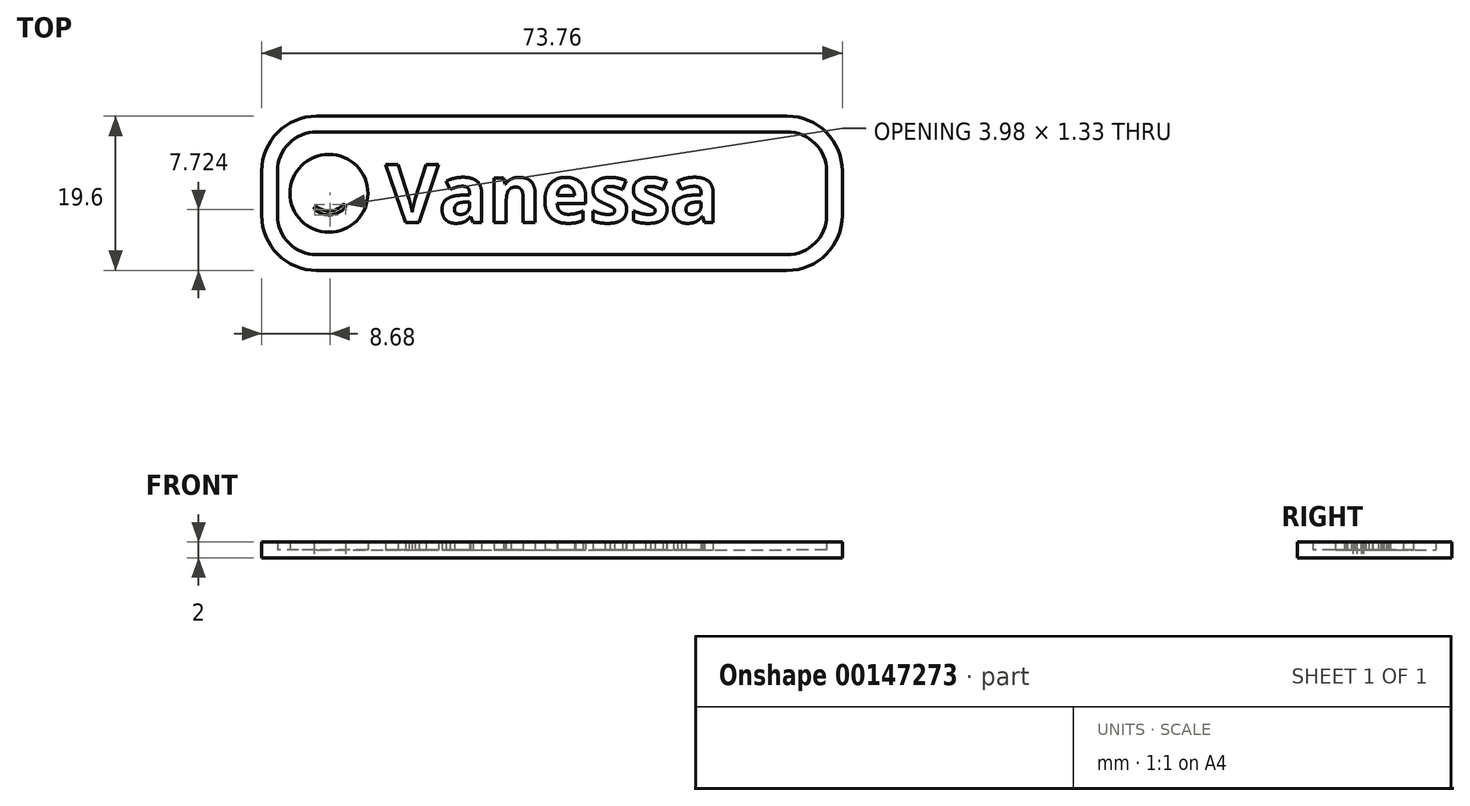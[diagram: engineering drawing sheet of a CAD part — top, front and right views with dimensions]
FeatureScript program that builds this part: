
annotation { "Feature Type Name" : "Feature", "Feature Type Description" : "" }
export const myFeature = defineFeature(function(context is Context, id is Id, definition is map)
    precondition{}
    {
        {
            var Q0;
            Q0=qCreatedBy(makeId("Top.planeOp"),FACE);
            var sketch = newSketch(context, id + "F0", { "sketchPlane" : qUnion([Q0])});
            skLineSegment(sketch, "E0.bottom", {"start": v(29.88, -7.8) * mm, "end": v(-29.88, -7.8) * mm});
            skLineSegment(sketch, "E0.top", {"start": v(29.88, 7.8) * mm, "end": v(-29.88, 7.8) * mm});
            skLineSegment(sketch, "E0.left", {"start": v(34.88, -2.8) * mm, "end": v(34.88, 2.8) * mm});
            skLineSegment(sketch, "E0.right", {"start": v(-34.88, -2.8) * mm, "end": v(-34.88, 2.8) * mm});
            skPoint(sketch, "E0.middle", {"position": v(0, 0) * mm});
            skPoint(sketch, "E1.visualSharp", {"position": v(-34.88, 7.8) * mm});
            skArc(sketch, "E1.filletArc", {"start": v(-29.88, 7.8) * mm, "mid": v(-33.41, 6.34) * mm, "end": v(-34.88, 2.8) * mm});
            skPoint(sketch, "E2.visualSharp", {"position": v(34.88, -7.8) * mm});
            skArc(sketch, "E2.filletArc", {"start": v(29.88, -7.8) * mm, "mid": v(33.41, -6.34) * mm, "end": v(34.88, -2.8) * mm});
            skPoint(sketch, "E3.visualSharp", {"position": v(34.88, 7.8) * mm});
            skArc(sketch, "E3.filletArc", {"start": v(34.88, 2.8) * mm, "mid": v(33.41, 6.34) * mm, "end": v(29.88, 7.8) * mm});
            skPoint(sketch, "E4.visualSharp", {"position": v(-34.88, -7.8) * mm});
            skArc(sketch, "E4.filletArc", {"start": v(-34.88, -2.8) * mm, "mid": v(-33.41, -6.34) * mm, "end": v(-29.88, -7.8) * mm});
            skLineSegment(sketch, "E5.0", {"start": v(29.88, 9.8) * mm, "end": v(-29.88, 9.8) * mm});
            skArc(sketch, "E5.1", {"start": v(36.88, 2.8) * mm, "mid": v(34.83, 7.75) * mm, "end": v(29.88, 9.8) * mm});
            skArc(sketch, "E5.2", {"start": v(-29.88, 9.8) * mm, "mid": v(-34.83, 7.75) * mm, "end": v(-36.88, 2.8) * mm});
            skLineSegment(sketch, "E5.3", {"start": v(36.88, -2.8) * mm, "end": v(36.88, 2.8) * mm});
            skLineSegment(sketch, "E5.4", {"start": v(-36.88, -2.8) * mm, "end": v(-36.88, 2.8) * mm});
            skArc(sketch, "E5.5", {"start": v(-36.88, -2.8) * mm, "mid": v(-34.83, -7.75) * mm, "end": v(-29.88, -9.8) * mm});
            skLineSegment(sketch, "E5.6", {"start": v(29.88, -9.8) * mm, "end": v(-29.88, -9.8) * mm});
            skArc(sketch, "E5.7", {"start": v(29.88, -9.8) * mm, "mid": v(34.83, -7.75) * mm, "end": v(36.88, -2.8) * mm});
            skText(sketch, "E6", { "text": "Vanessa", "fontName": "OpenSans-Bold.ttf"});
            skLineSegment(sketch, "E7", {"start": v(-21.12, 0) * mm, "end": v(21.12, 0) * mm, "construction": true});
            skCircle(sketch, "E8", {"center": v(-28.33, 0) * mm, "radius": 4.35 * mm});
            skLineSegment(sketch, "E9", {"start": v(-32.35, 1.65) * mm, "end": v(-24.3, 1.65) * mm, "construction": true});
            skCircle(sketch, "E10", {"center": v(-30.35, 1.65) * mm, "radius": 0.6 * mm});
            skCircle(sketch, "E11", {"center": v(-26.23, 1.65) * mm, "radius": 0.6 * mm});
            skArc(sketch, "E12", {"start": v(-26.46, -1.66) * mm, "mid": v(-28.15, -2.5) * mm, "end": v(-29.94, -1.9) * mm});
            skArc(sketch, "E13.0.startCap", {"start": v(-26.64, -1.5) * mm, "mid": v(-26.3, -1.47) * mm, "end": v(-26.27, -1.82) * mm});
            skArc(sketch, "E13.0.endCap", {"start": v(-30.1, -2.1) * mm, "mid": v(-30.13, -1.75) * mm, "end": v(-29.78, -1.72) * mm});
            skArc(sketch, "E13.0.left", {"start": v(-26.27, -1.82) * mm, "mid": v(-28.13, -2.74) * mm, "end": v(-30.1, -2.1) * mm});
            skArc(sketch, "E13.0.right", {"start": v(-26.64, -1.5) * mm, "mid": v(-28.17, -2.24) * mm, "end": v(-29.78, -1.72) * mm});
            skCircle(sketch, "E14", {"center": v(-28.33, 0) * mm, "radius": 4.95 * mm});
            const initialGuessF0  = {"E6": [-0.02112, -0.00372, 1, 0, 0.00744]};
            skSetInitialGuess(sketch, initialGuessF0);
            skSolve(sketch);
        }
        {
            var Q0;
            Q0=makeQuery(id+"F0.imprint","IMPRINT",FACE,{"disambiguationData":[TD([[makeQuery(id+"F0.imprint","IMPRINT",EDGE,{"derivedFrom":sQuery(id+"F0.wireOp",EDGE,"E0.bottom")}),1.0]])]});
            var Q1;
            Q1 = qSketchRegion(id + "F0", true);
            var Q2;
            Q2=makeQuery(id+"F0.imprint","IMPRINT",FACE,{"disambiguationData":[TD([[makeQuery(id+"F0.imprint","IMPRINT",EDGE,{"derivedFrom":sQuery(id+"F0.wireOp",EDGE,"E6.sketch_text.stroke-35")}),-1.0]])]});
            var Q3;
            Q3=makeQuery(id+"F0.imprint","IMPRINT",FACE,{"disambiguationData":[TD([[makeQuery(id+"F0.imprint","IMPRINT",EDGE,{"derivedFrom":sQuery(id+"F0.wireOp",EDGE,"E6.sketch_text.stroke-142")}),1.0]])]});
            var Q4;
            Q4=makeQuery(id+"F0.imprint","IMPRINT",FACE,{"disambiguationData":[TD([[makeQuery(id+"F0.imprint","IMPRINT",EDGE,{"derivedFrom":sQuery(id+"F0.wireOp",EDGE,"E6.sketch_text.stroke-52")}),-1.0]])]});
            var Q5;
            Q5=makeQuery(id+"F0.imprint","IMPRINT",FACE,{"disambiguationData":[TD([[makeQuery(id+"F0.imprint","IMPRINT",EDGE,{"derivedFrom":sQuery(id+"F0.wireOp",EDGE,"E8")}),1.0]])]});
            var Q6;
            Q6=makeQuery(id+"F0.imprint","IMPRINT",FACE,{"disambiguationData":[TD([[makeQuery(id+"F0.imprint","IMPRINT",EDGE,{"derivedFrom":sQuery(id+"F0.wireOp",EDGE,"E6.sketch_text.stroke-98")}),-1.0]])]});
            var Q7;
            Q7=makeQuery(id+"F0.imprint","IMPRINT",FACE,{"disambiguationData":[TD([[makeQuery(id+"F0.imprint","IMPRINT",EDGE,{"derivedFrom":sQuery(id+"F0.wireOp",EDGE,"E6.sketch_text.stroke-28")}),1.0]])]});
            var Q8;
            Q8=makeQuery(id+"F0.imprint","IMPRINT",FACE,{"disambiguationData":[TD([[makeQuery(id+"F0.imprint","IMPRINT",EDGE,{"derivedFrom":sQuery(id+"F0.wireOp",EDGE,"E6.sketch_text.stroke-10")}),-1.0]])]});
            var Q9;
            Q9=makeQuery(id+"F0.imprint","IMPRINT",FACE,{"disambiguationData":[TD([[makeQuery(id+"F0.imprint","IMPRINT",EDGE,{"derivedFrom":sQuery(id+"F0.wireOp",EDGE,"E0.bottom")}),-1.0]])]});
            var Q10;
            Q10=makeQuery(id+"F0.imprint","IMPRINT",FACE,{"disambiguationData":[TD([[makeQuery(id+"F0.imprint","IMPRINT",EDGE,{"derivedFrom":sQuery(id+"F0.wireOp",EDGE,"E6.sketch_text.stroke-0")}),-1.0]])]});
            var Q11;
            Q11=makeQuery(id+"F0.imprint","IMPRINT",FACE,{"disambiguationData":[TD([[makeQuery(id+"F0.imprint","IMPRINT",EDGE,{"derivedFrom":sQuery(id+"F0.wireOp",EDGE,"E6.sketch_text.stroke-124")}),-1.0]])]});
            var Q12;
            Q12=makeQuery(id+"F0.imprint","IMPRINT",FACE,{"disambiguationData":[TD([[makeQuery(id+"F0.imprint","IMPRINT",EDGE,{"derivedFrom":sQuery(id+"F0.wireOp",EDGE,"E8")}),-1.0]])]});
            var Q13;
            Q13=makeQuery(id+"F0.imprint","IMPRINT",FACE,{"disambiguationData":[TD([[makeQuery(id+"F0.imprint","IMPRINT",EDGE,{"derivedFrom":sQuery(id+"F0.wireOp",EDGE,"E6.sketch_text.stroke-72")}),-1.0]])]});
            var Q14;
            Q14=makeQuery(id+"F0.imprint","IMPRINT",FACE,{"disambiguationData":[TD([[makeQuery(id+"F0.imprint","IMPRINT",EDGE,{"derivedFrom":sQuery(id+"F0.wireOp",EDGE,"E6.sketch_text.stroke-52")}),1.0]])]});
            var Q15;
            Q15=makeQuery(id+"F0.imprint","IMPRINT",FACE,{"disambiguationData":[TD([[makeQuery(id+"F0.imprint","IMPRINT",EDGE,{"derivedFrom":sQuery(id+"F0.wireOp",EDGE,"E13.0.startCap")}),-1.0]])]});
            var Q16;
            Q16=makeQuery(id+"F0.imprint","IMPRINT",FACE,{"disambiguationData":[TD([[makeQuery(id+"F0.imprint","IMPRINT",EDGE,{"derivedFrom":sQuery(id+"F0.wireOp",EDGE,"E10")}),1.0]])]});
            var Q17;
            Q17=makeQuery(id+"F0.imprint","IMPRINT",FACE,{"disambiguationData":[TD([[makeQuery(id+"F0.imprint","IMPRINT",EDGE,{"derivedFrom":sQuery(id+"F0.wireOp",EDGE,"E11")}),1.0]])]});
            extrude(context, id + "F1", {"entities" : qUnion([Q0, Q1, Q2, Q3, Q4, Q5, Q6, Q7, Q8, Q9, Q10, Q11, Q12, Q13, Q14, Q15, Q16, Q17]), "depth" : 1 * mm, "offsetDistance" : 25 * mm});
        }
        {
            var Q0;
            Q0=makeQuery(id+"F0.imprint","IMPRINT",FACE,{"disambiguationData":[TD([[makeQuery(id+"F0.imprint","IMPRINT",EDGE,{"derivedFrom":sQuery(id+"F0.wireOp",EDGE,"E0.bottom")}),1.0]])]});
            var Q1;
            Q1=makeQuery(id+"F0.imprint","IMPRINT",FACE,{"disambiguationData":[TD([[makeQuery(id+"F0.imprint","IMPRINT",EDGE,{"derivedFrom":sQuery(id+"F0.wireOp",EDGE,"E8")}),-1.0]])]});
            var Q2;
            Q2=makeQuery(id+"F0.imprint","IMPRINT",FACE,{"disambiguationData":[TD([[makeQuery(id+"F0.imprint","IMPRINT",EDGE,{"derivedFrom":sQuery(id+"F0.wireOp",EDGE,"E13.0.startCap")}),-1.0]])]});
            var Q3;
            Q3=makeQuery(id+"F0.imprint","IMPRINT",FACE,{"disambiguationData":[TD([[makeQuery(id+"F0.imprint","IMPRINT",EDGE,{"derivedFrom":sQuery(id+"F0.wireOp",EDGE,"E10")}),1.0]])]});
            var Q4;
            Q4=makeQuery(id+"F0.imprint","IMPRINT",FACE,{"disambiguationData":[TD([[makeQuery(id+"F0.imprint","IMPRINT",EDGE,{"derivedFrom":sQuery(id+"F0.wireOp",EDGE,"E11")}),1.0]])]});
            var Q5;
            Q5=makeQuery(id+"F0.imprint","IMPRINT",FACE,{"disambiguationData":[TD([[makeQuery(id+"F0.imprint","IMPRINT",EDGE,{"derivedFrom":sQuery(id+"F0.wireOp",EDGE,"E6.sketch_text.stroke-0")}),-1.0]])]});
            var Q6;
            Q6=makeQuery(id+"F0.imprint","IMPRINT",FACE,{"disambiguationData":[TD([[makeQuery(id+"F0.imprint","IMPRINT",EDGE,{"derivedFrom":sQuery(id+"F0.wireOp",EDGE,"E6.sketch_text.stroke-10")}),-1.0]])]});
            var Q7;
            Q7=makeQuery(id+"F0.imprint","IMPRINT",FACE,{"disambiguationData":[TD([[makeQuery(id+"F0.imprint","IMPRINT",EDGE,{"derivedFrom":sQuery(id+"F0.wireOp",EDGE,"E6.sketch_text.stroke-35")}),-1.0]])]});
            var Q8;
            Q8=makeQuery(id+"F0.imprint","IMPRINT",FACE,{"disambiguationData":[TD([[makeQuery(id+"F0.imprint","IMPRINT",EDGE,{"derivedFrom":sQuery(id+"F0.wireOp",EDGE,"E6.sketch_text.stroke-52")}),-1.0]])]});
            var Q9;
            Q9=makeQuery(id+"F0.imprint","IMPRINT",FACE,{"disambiguationData":[TD([[makeQuery(id+"F0.imprint","IMPRINT",EDGE,{"derivedFrom":sQuery(id+"F0.wireOp",EDGE,"E6.sketch_text.stroke-72")}),-1.0]])]});
            var Q10;
            Q10=makeQuery(id+"F0.imprint","IMPRINT",FACE,{"disambiguationData":[TD([[makeQuery(id+"F0.imprint","IMPRINT",EDGE,{"derivedFrom":sQuery(id+"F0.wireOp",EDGE,"E6.sketch_text.stroke-98")}),-1.0]])]});
            var Q11;
            Q11=makeQuery(id+"F0.imprint","IMPRINT",FACE,{"disambiguationData":[TD([[makeQuery(id+"F0.imprint","IMPRINT",EDGE,{"derivedFrom":sQuery(id+"F0.wireOp",EDGE,"E6.sketch_text.stroke-124")}),-1.0]])]});
            extrude(context, id + "F2", {"entities" : qUnion([Q0, Q1, Q2, Q3, Q4, Q5, Q6, Q7, Q8, Q9, Q10, Q11]), "operationType" : NewBodyOperationType.ADD, "depth" : 2 * mm, "offsetDistance" : 25 * mm});
        }
    });
